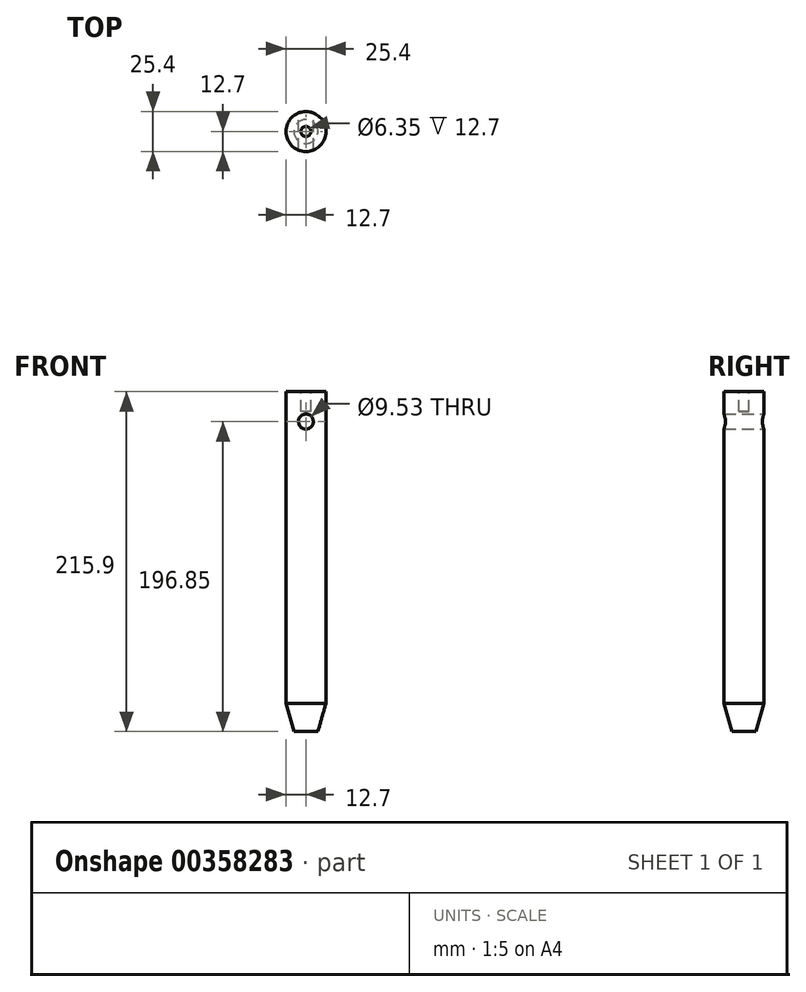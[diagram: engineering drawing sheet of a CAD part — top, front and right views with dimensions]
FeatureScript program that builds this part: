
annotation { "Feature Type Name" : "Feature", "Feature Type Description" : "" }
export const myFeature = defineFeature(function(context is Context, id is Id, definition is map)
    precondition{}
    {
        {
            var Q0;
            Q0=qCreatedBy(makeId("Top.planeOp"),FACE);
            var sketch = newSketch(context, id + "F0", { "sketchPlane" : qUnion([Q0])});
            skCircle(sketch, "E0", {"center": v(0, 0) * mm, "radius": 12.7 * mm});
            skSolve(sketch);
        }
        {
            var Q0;
            Q0 = qSketchRegion(id + "F0", true);
            extrude(context, id + "F1", {"entities" : qUnion([Q0]), "offsetDistance" : 25.4 * mm, "depth" : 215.9 * mm});
        }
        {
            var Q0;
            Q0=makeQuery(id+"F1.opExtrude","CAP_EDGE",EDGE,{"disambiguationData":[OSD([sQuery(id+"F0.wireOp",EDGE,"E0")])],"isStart":true});
            chamfer(context, id + "F2", {"entities" : qUnion([Q0]), "chamferType" : ChamferType.TWO_OFFSETS, "width1" : 17.78 * mm, "oppositeDirection" : false, "width2" : 5.08 * mm, "tangentPropagation" : true});
        }
        {
            var Q0;
            Q0=qCreatedBy(makeId("Front.planeOp"),FACE);
            var sketch = newSketch(context, id + "F3", { "sketchPlane" : qUnion([Q0])});
            skCircle(sketch, "E1", {"center": v(0, 196.85) * mm, "radius": 4.76 * mm});
            skSolve(sketch);
        }
        {
            var Q0;
            Q0 = qSketchRegion(id + "F3", true);
            extrude(context, id + "F4", {"entities" : qUnion([Q0]), "operationType" : NewBodyOperationType.REMOVE, "depth" : 25.4 * mm, "hasSecondDirection" : true, "secondDirectionOppositeDirection" : true, "secondDirectionDepth" : 25.4 * mm});
        }
        {
            var Q0;
            Q0=makeQuery(id+"F1.opExtrude","CAP_FACE",FACE,{"disambiguationData":[OSD([sQuery(id+"F0.wireOp",EDGE,"E0")])],"isStart":false});
            var sketch = newSketch(context, id + "F5", { "sketchPlane" : qUnion([Q0])});
            skCircle(sketch, "E2", {"center": v(0, 0) * mm, "radius": 3.18 * mm});
            skSolve(sketch);
        }
        {
            var Q0;
            Q0 = qSketchRegion(id + "F5", true);
            extrude(context, id + "F6", {"entities" : qUnion([Q0]), "operationType" : NewBodyOperationType.REMOVE, "oppositeDirection" : true, "depth" : 12.7 * mm});
        }
    });
